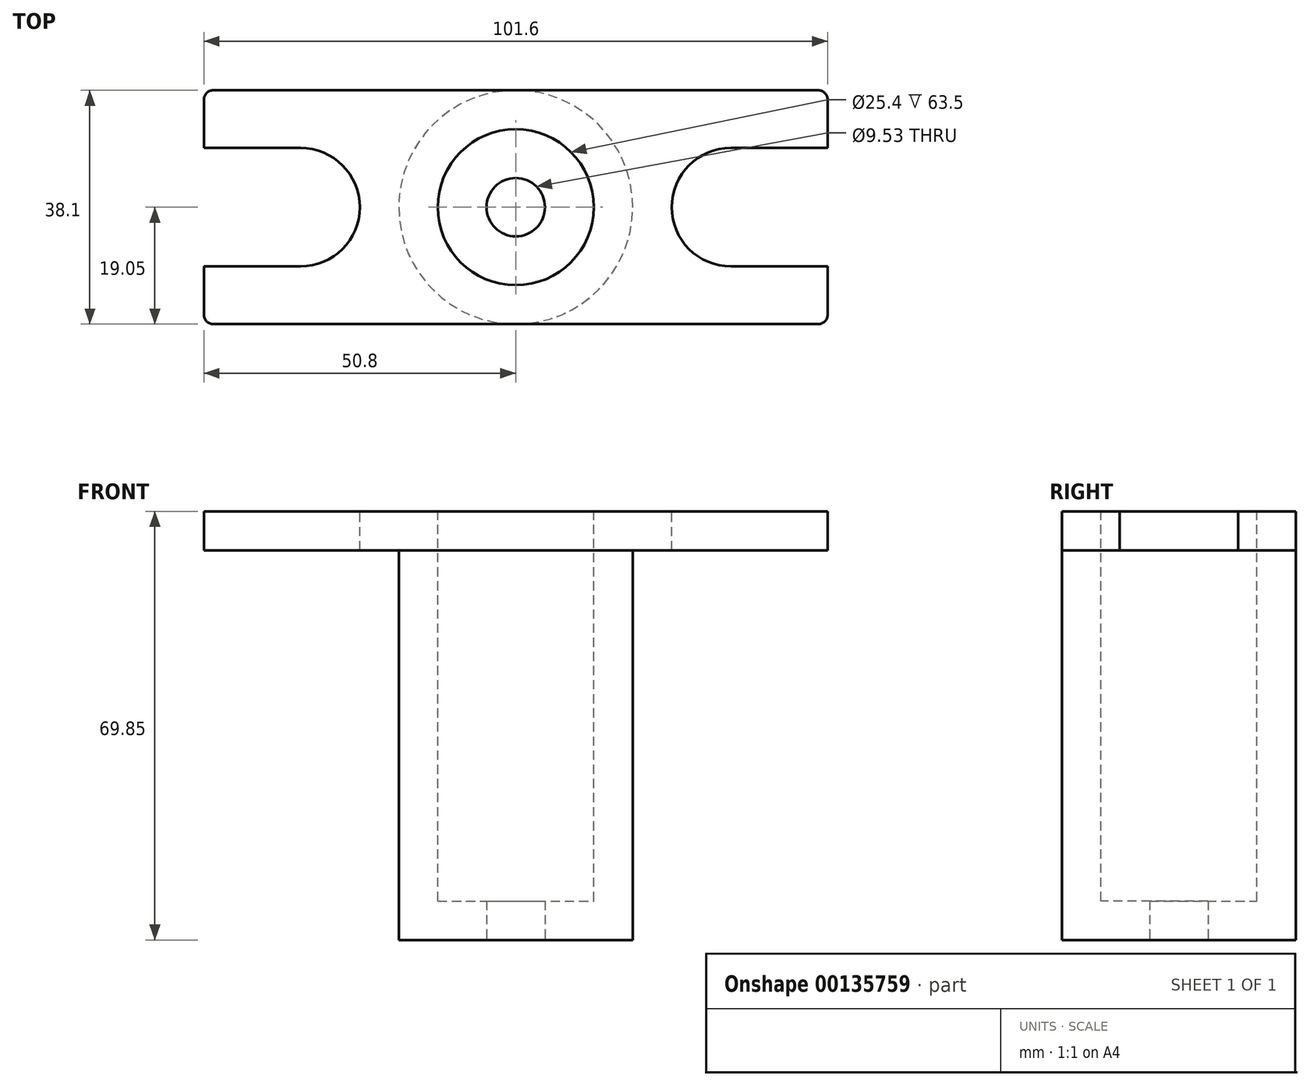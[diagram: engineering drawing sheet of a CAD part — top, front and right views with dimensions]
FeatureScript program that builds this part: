
annotation { "Feature Type Name" : "Feature", "Feature Type Description" : "" }
export const myFeature = defineFeature(function(context is Context, id is Id, definition is map)
    precondition{}
    {
        {
            var Q0;
            Q0=qCreatedBy(makeId("Top.planeOp"),FACE);
            var sketch = newSketch(context, id + "F0", { "sketchPlane" : qUnion([Q0])});
            skCircle(sketch, "E0", {"center": v(0, 0) * mm, "radius": 12.7 * mm});
            skLineSegment(sketch, "E1.bottom", {"start": v(50.8, -19.05) * mm, "end": v(-50.8, -19.05) * mm});
            skLineSegment(sketch, "E1.top", {"start": v(50.8, 19.05) * mm, "end": v(-50.8, 19.05) * mm});
            skLineSegment(sketch, "E1.left", {"start": v(50.8, -19.05) * mm, "end": v(50.8, 19.05) * mm});
            skLineSegment(sketch, "E1.right", {"start": v(-50.8, -19.05) * mm, "end": v(-50.8, 19.05) * mm});
            skSolve(sketch);
        }
        {
            var Q0;
            Q0=makeQuery(id+"F0.imprint","IMPRINT",FACE,{"disambiguationData":[TD([[makeQuery(id+"F0.imprint","IMPRINT",EDGE,{"derivedFrom":sQuery(id+"F0.wireOp",EDGE,"E0")}),-1.0]])]});
            extrude(context, id + "F1", {"entities" : qUnion([Q0]), "oppositeDirection" : true, "depth" : 6.35 * mm});
        }
        {
            var Q0;
            Q0=makeQuery(id+"F0.imprint","IMPRINT",FACE,{"disambiguationData":[TD([[makeQuery(id+"F0.imprint","IMPRINT",EDGE,{"derivedFrom":sQuery(id+"F0.wireOp",EDGE,"E0")}),-1.0]])]});
            var sketch = newSketch(context, id + "F2", { "sketchPlane" : qUnion([Q0])});
            skCircle(sketch, "E2", {"center": v(0, 0) * mm, "radius": 19.05 * mm});
            skSolve(sketch);
        }
        {
            var Q0;
            Q0=makeQuery(id+"F2.imprint","IMPRINT",FACE,{"disambiguationData":[TD([[makeQuery(id+"F2.imprint","IMPRINT",EDGE,{"derivedFrom":makeQuery(id+"F0.imprint","IMPRINT",EDGE,{"derivedFrom":sQuery(id+"F0.wireOp",EDGE,"E0")})}),-1.0]])]});
            extrude(context, id + "F3", {"entities" : qUnion([Q0]), "operationType" : NewBodyOperationType.ADD, "oppositeDirection" : true, "depth" : 69.85 * mm});
        }
        {
            var Q0;
            Q0=makeQuery(id+"F1.opExtrude","CAP_FACE",FACE,{"disambiguationData":[OSD([sQuery(id+"F0.wireOp",EDGE,"E0"),sQuery(id+"F0.wireOp",EDGE,"E1.bottom"),sQuery(id+"F0.wireOp",EDGE,"E1.top"),sQuery(id+"F0.wireOp",EDGE,"E1.left"),sQuery(id+"F0.wireOp",EDGE,"E1.right")])],"isStart":true});
            var sketch = newSketch(context, id + "F4", { "sketchPlane" : qUnion([Q0])});
            skArc(sketch, "E3", {"start": v(-35.05, -9.65) * mm, "mid": v(-25.4, 0) * mm, "end": v(-35.05, 9.65) * mm});
            skLineSegment(sketch, "E4", {"start": v(-35.05, 9.65) * mm, "end": v(-50.8, 9.65) * mm});
            skLineSegment(sketch, "E5", {"start": v(-35.05, -9.65) * mm, "end": v(-50.8, -9.65) * mm});
            skLineSegment(sketch, "E6.MirrorCS", {"start": v(35.05, 9.65) * mm, "end": v(50.8, 9.65) * mm});
            skArc(sketch, "E7.MirrorCS", {"start": v(35.05, -9.65) * mm, "mid": v(25.4, 0) * mm, "end": v(35.05, 9.65) * mm});
            skLineSegment(sketch, "E8.MirrorCS", {"start": v(35.05, -9.65) * mm, "end": v(50.8, -9.65) * mm});
            skSolve(sketch);
        }
        {
            var Q0;
            Q0=makeQuery(id+"F4.imprint","IMPRINT",FACE,{"disambiguationData":[TD([[makeQuery(id+"F4.imprint","IMPRINT",EDGE,{"derivedFrom":sQuery(id+"F4.wireOp",EDGE,"E3")}),1.0]])]});
            var Q1;
            {var subQ0=sQuery(id+"F4.wireOp",EDGE,"E6.MirrorCS");Q1=makeQuery(id+"F4.imprint","IMPRINT",FACE,{"disambiguationData":[TD([[makeQuery(id+"F4.imprint","IMPRINT",EDGE,{"derivedFrom":subQ0}),-1.0]])]});}
            extrude(context, id + "F5", {"entities" : qUnion([Q0, Q1]), "operationType" : NewBodyOperationType.REMOVE, "oppositeDirection" : true, "depth" : 25.4 * mm});
        }
        {
            var Q0;
            Q0=makeQuery(id+"F1.opExtrude","SWEPT_EDGE",EDGE,{"disambiguationData":[OSD([sQuery(id+"F0.wireOp",EDGE,"E1.top"),sQuery(id+"F0.wireOp",EDGE,"E1.right")])]});
            var Q1;
            Q1=makeQuery(id+"F1.opExtrude","SWEPT_EDGE",EDGE,{"disambiguationData":[OSD([sQuery(id+"F0.wireOp",EDGE,"E1.bottom"),sQuery(id+"F0.wireOp",EDGE,"E1.right")])]});
            var Q2;
            Q2=makeQuery(id+"F1.opExtrude","SWEPT_EDGE",EDGE,{"disambiguationData":[OSD([sQuery(id+"F0.wireOp",EDGE,"E1.bottom"),sQuery(id+"F0.wireOp",EDGE,"E1.left")])]});
            var Q3;
            Q3=makeQuery(id+"F1.opExtrude","SWEPT_EDGE",EDGE,{"disambiguationData":[OSD([sQuery(id+"F0.wireOp",EDGE,"E1.top"),sQuery(id+"F0.wireOp",EDGE,"E1.left")])]});
            fillet(context, id + "F6", {"entities" : qUnion([Q0, Q1, Q2, Q3]), "radius" : 1.52 * mm, "tangentPropagation" : true, "allowEdgeOverflow" : false});
        }
        {
            var Q0;
            Q0=makeQuery(id+"F3.opExtrude","CAP_FACE",FACE,{"disambiguationData":[OSD([sQuery(id+"F0.wireOp",EDGE,"E0"),sQuery(id+"F2.wireOp",EDGE,"E2")])],"isStart":false});
            var sketch = newSketch(context, id + "F7", { "sketchPlane" : qUnion([Q0])});
            skCircle(sketch, "E9", {"center": v(0, 0) * mm, "radius": 19.05 * mm});
            skCircle(sketch, "E10", {"center": v(0, 0) * mm, "radius": 4.76 * mm});
            skSolve(sketch);
        }
        {
            var Q0;
            Q0=makeQuery(id+"F7.imprint","IMPRINT",FACE,{"disambiguationData":[TD([[makeQuery(id+"F7.imprint","IMPRINT",EDGE,{"derivedFrom":sQuery(id+"F7.wireOp",EDGE,"E10")}),-1.0]])]});
            extrude(context, id + "F8", {"entities" : qUnion([Q0]), "operationType" : NewBodyOperationType.ADD, "oppositeDirection" : true, "depth" : 6.35 * mm});
        }
    });
